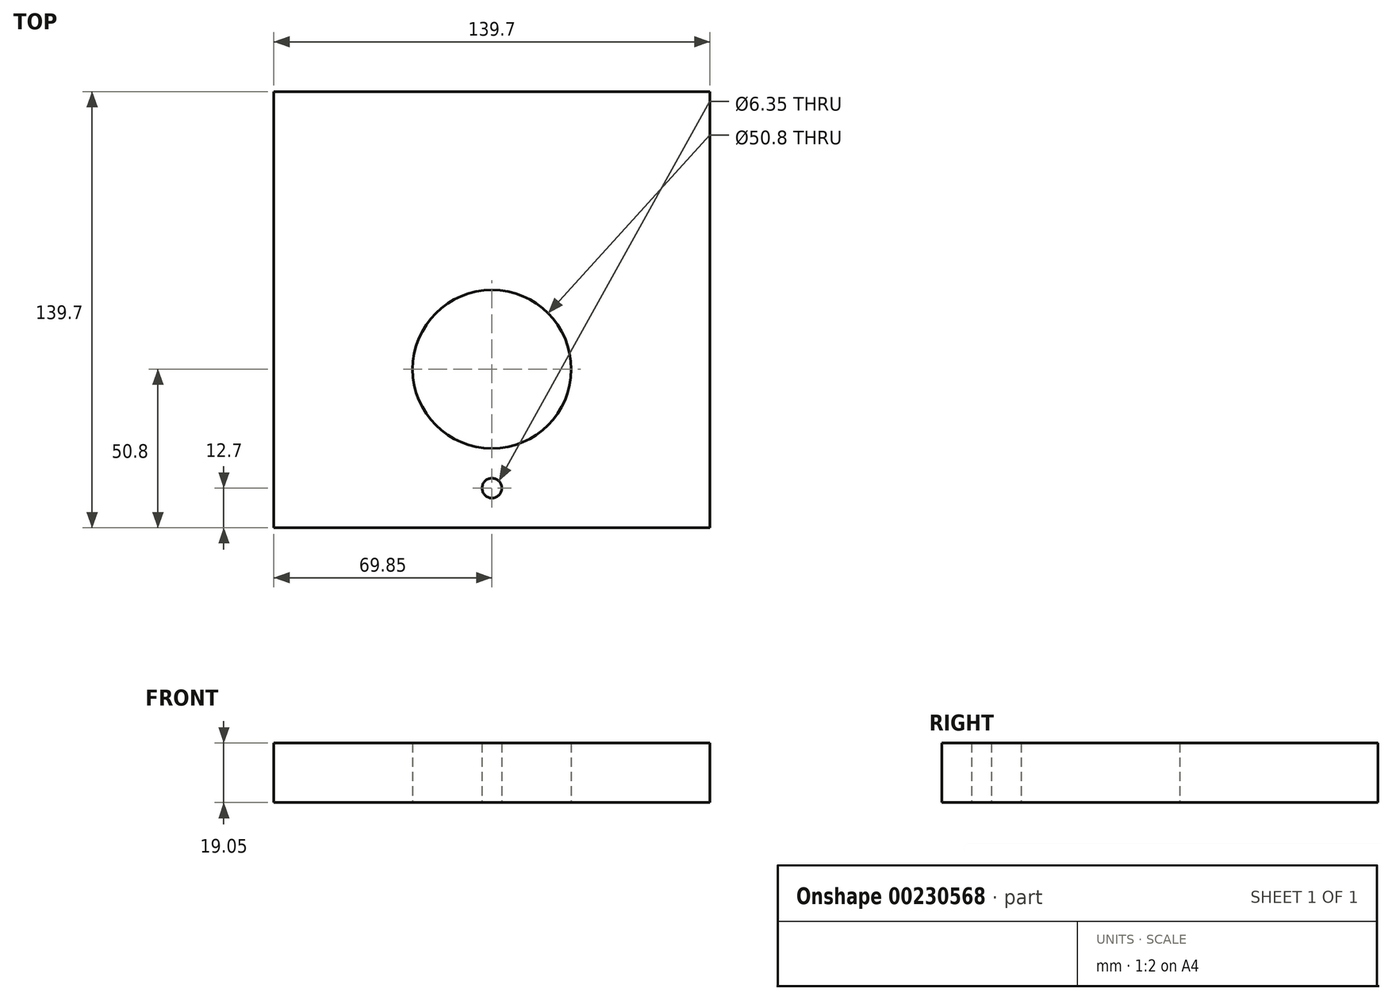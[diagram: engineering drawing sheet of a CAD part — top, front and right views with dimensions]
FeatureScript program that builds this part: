
annotation { "Feature Type Name" : "Feature", "Feature Type Description" : "" }
export const myFeature = defineFeature(function(context is Context, id is Id, definition is map)
    precondition{}
    {
        {
            var Q0;
            Q0=qCreatedBy(makeId("Top.planeOp"),FACE);
            var sketch = newSketch(context, id + "F0", { "sketchPlane" : qUnion([Q0])});
            skLineSegment(sketch, "E0.bottom", {"start": v(69.85, 69.85) * mm, "end": v(-69.85, 69.85) * mm});
            skLineSegment(sketch, "E0.top", {"start": v(69.85, -69.85) * mm, "end": v(-69.85, -69.85) * mm});
            skLineSegment(sketch, "E0.left", {"start": v(69.85, 69.85) * mm, "end": v(69.85, -69.85) * mm});
            skLineSegment(sketch, "E0.right", {"start": v(-69.85, 69.85) * mm, "end": v(-69.85, -69.85) * mm});
            skPoint(sketch, "E0.middle", {"position": v(0, 0) * mm});
            skLineSegment(sketch, "E1", {"start": v(0, -69.85) * mm, "end": v(0, -57.15) * mm});
            skLineSegment(sketch, "E2", {"start": v(0, -57.15) * mm, "end": v(0, -19.05) * mm});
            skCircle(sketch, "E3", {"center": v(0, -57.15) * mm, "radius": 3.18 * mm});
            skCircle(sketch, "E4", {"center": v(0, -19.05) * mm, "radius": 25.4 * mm});
            skSolve(sketch);
        }
        {
            var Q0;
            Q0 = qSketchRegion(id + "F0", true);
            extrude(context, id + "F1", {"entities" : qUnion([Q0]), "depth" : 19.05 * mm});
        }
    });
